# Revit family: Deca_Cuba de apoio quadrada_Cubas Apoio_L.737
name_source: partatom
category: Plumbing Fixtures
units: mm (PartAtom-declared; Revit-internal decimal feet)

## family parameters
Cut with Voids When Loaded = Yes
Host = Face
Part Type = Normal
Room Calculation Point = No
Round Connector Dimension = Use Radius
Shared = No

## types (7) — shared parameters
Acompanha o Produto = -
Aprovado por = quattroD
Atendimento ao Cliente = 0800-0117073
Categoria = CUBAS
Composição Anel Vedação = -
Composição Assento = -
Composição Básica = Argila, feldspato, caulim, vidrados e corantes inorgânicos.
Composição Componente = Não Possui
Consumo = -
Cor Interna = -
Cor Secundária = -
Cores Componente = Não Possui
Criado por = quattroD
Código Pai = L.737
Description = Cuba de apoio quadrada
Diâmetro Ponto de Esgoto = 0.03 m
Informações Complementares = -
Itens de Instalação = 1601.C; 1601.C.CLI; 1602.C; 1602.C.PLA; 1680.C.100.112; 1682.C.100.112; 1684.C.100.112
Linha = Cubas Apoio
Manufacturer = Deca
Norma = NBR-16728-1;NBR-16728-2
Peso Líquido (Kg) = 12.52
Pressão máx. funcionamento = -
Pressão mín. Aquec. Acúmulo = -
Pressão mín. Aquec. Passagem = -
Pressão mín. funcionamento = -
Raio Ponto de Esgoto = 0.01 m
Saída de Esgoto = Válvula Curta
Segmento = Banheiro Luxo
Tipo de dispositivo economizador = -
Tipo de mecanismo utilizado = -
Tipo de rosca de entrada = -
Tipo de rosca de saída = -
URL = www.deca.com.br
Vazão na Pressão máx. (L/min) = -
Vazão na Pressão mín. (L/min) = -
zero-valued in all types: Default Elevation

## per-type parameters (varying)
| type | Cor Principal | Material | Model |
| L.737.17_Branco | Branco | Deca_Branco | L.737.17 |
| L.737.22_Marrom Fosco | Marrom Fosco | Deca_Marrom Fosco | L.737.22 |
| L.737.40_Vanilla | Vanilla | Deca_Vanilla | L.737.40 |
| L.737.41_Rose Millennial | Rose Millennial | Deca_Rose Milennial | L.737.41 |
| L.737.42_Kale Green | Kale Green | Deca_Kale Green | L.737.42 |
| L.737.43_Navy Blue | Navy Blue | Deca_Navy Blue | L.737.43 |
| L.737.94_Ébano Fosco | Ébano Fosco | Deca_Ébano Fosco | L.737.94 |

## geometry (parser evidence)
native form markers: Sweep x3
no freeform markers — native parametric forms only
